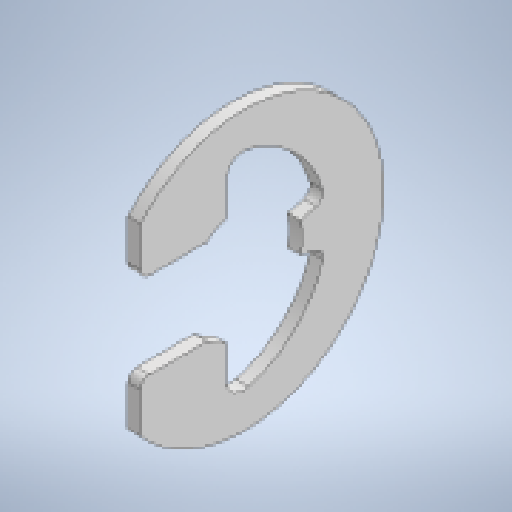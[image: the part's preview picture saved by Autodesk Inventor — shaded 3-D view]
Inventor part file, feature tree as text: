
AUTODESK INVENTOR PART (.ipt)
format: ipt  version: 2023 (Build 270158030, 158C)  size: 157,696 bytes
history: native  units: in
note: dims shown in document units (in); Inventor stores cm internally (conversion verified against a paired STEP export)
features: fillet x1
ambient origin geometry x8: Origin, YZ Plane, XZ Plane, XY Plane, X Axis, Y Axis, Z Axis, Center Point
bodies: Solid1 (feature_tree)
feature tree (1):
  fillet  "Fillet2"  [1 undecoded]
note: 1 required parameter value undecoded (feature->parameter linkage not recoverable at this tier; creation-order binding heuristic only, values carry confidence <= 0.55)
